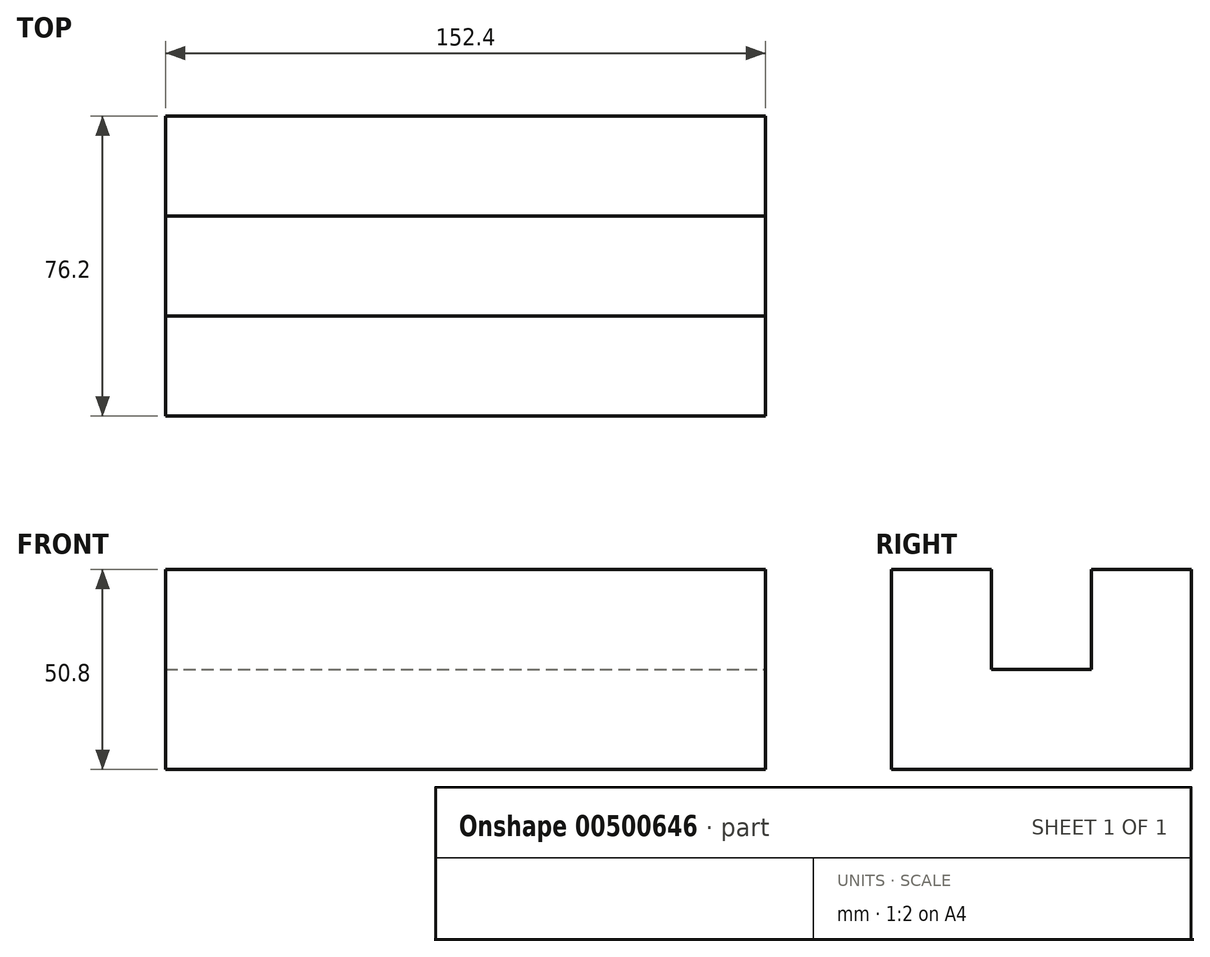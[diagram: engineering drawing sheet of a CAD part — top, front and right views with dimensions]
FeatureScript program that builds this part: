
annotation { "Feature Type Name" : "Feature", "Feature Type Description" : "" }
export const myFeature = defineFeature(function(context is Context, id is Id, definition is map)
    precondition{}
    {
        {
            var Q0;
            Q0=qCreatedBy(makeId("Top.planeOp"),FACE);
            var sketch = newSketch(context, id + "F0", { "sketchPlane" : qUnion([Q0])});
            skLineSegment(sketch, "E0.bottom", {"start": v(-74.97, 38.81) * mm, "end": v(77.43, 38.81) * mm});
            skLineSegment(sketch, "E0.top", {"start": v(-74.97, -37.39) * mm, "end": v(77.43, -37.39) * mm});
            skLineSegment(sketch, "E0.left", {"start": v(-74.97, 38.81) * mm, "end": v(-74.97, -37.39) * mm});
            skLineSegment(sketch, "E0.right", {"start": v(77.43, 38.81) * mm, "end": v(77.43, -37.39) * mm});
            skLineSegment(sketch, "E1.bottom", {"start": v(-74.97, -11.99) * mm, "end": v(77.43, -11.99) * mm});
            skLineSegment(sketch, "E1.left", {"start": v(-74.97, -11.99) * mm, "end": v(-74.97, -37.39) * mm});
            skLineSegment(sketch, "E1.right", {"start": v(77.43, -11.99) * mm, "end": v(77.43, -37.39) * mm});
            skLineSegment(sketch, "E2.bottom", {"start": v(77.43, 13.41) * mm, "end": v(-74.97, 13.41) * mm});
            skLineSegment(sketch, "E2.top", {"start": v(77.43, 38.81) * mm, "end": v(-74.97, 38.81) * mm});
            skLineSegment(sketch, "E2.left", {"start": v(77.43, 13.41) * mm, "end": v(77.43, 38.81) * mm});
            skLineSegment(sketch, "E2.right", {"start": v(-74.97, 13.41) * mm, "end": v(-74.97, 38.81) * mm});
            skSolve(sketch);
        }
        {
            var Q0;
            Q0=makeQuery(id+"F0.imprint","IMPRINT",FACE,{"disambiguationData":[TD([[makeQuery(id+"F0.imprint","IMPRINT",EDGE,{"derivedFrom":sQuery(id+"F0.wireOp",EDGE,"E1.bottom")}),-1.0]])]});
            extrude(context, id + "F1", {"entities" : qUnion([Q0]), "depth" : 50.8 * mm});
        }
        {
            var Q0;
            Q0=makeQuery(id+"F0.imprint","IMPRINT",FACE,{"disambiguationData":[TD([[makeQuery(id+"F0.imprint","IMPRINT",EDGE,{"derivedFrom":sQuery(id+"F0.wireOp",EDGE,"E0.left")}),1.0]])]});
            extrude(context, id + "F2", {"entities" : qUnion([Q0]), "operationType" : NewBodyOperationType.ADD, "depth" : 25.4 * mm});
        }
        {
            var Q0;
            Q0=makeQuery(id+"F0.imprint","IMPRINT",FACE,{"disambiguationData":[TD([[makeQuery(id+"F0.imprint","IMPRINT",EDGE,{"derivedFrom":sQuery(id+"F0.wireOp",EDGE,"E2.bottom")}),-1.0]])]});
            extrude(context, id + "F3", {"entities" : qUnion([Q0]), "operationType" : NewBodyOperationType.ADD, "depth" : 50.8 * mm});
        }
    });
